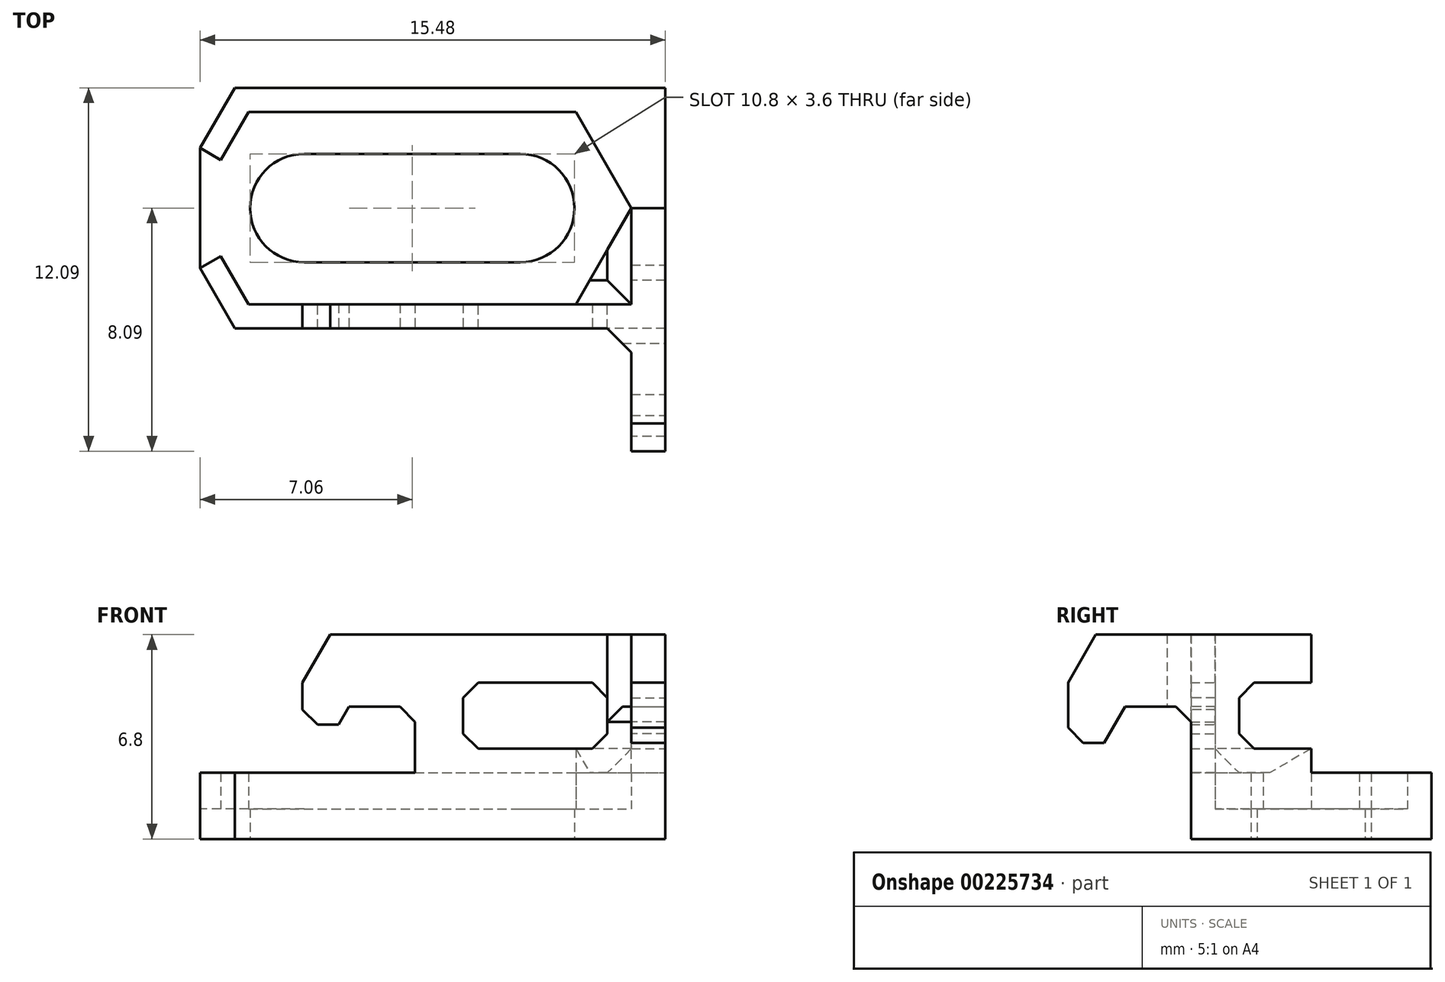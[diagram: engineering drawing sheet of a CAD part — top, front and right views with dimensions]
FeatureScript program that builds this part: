
annotation { "Feature Type Name" : "Feature", "Feature Type Description" : "" }
export const myFeature = defineFeature(function(context is Context, id is Id, definition is map)
    precondition{}
    {
        {
            var Q0;
            Q0=qCreatedBy(makeId("Top.planeOp"),FACE);
            var sketch = newSketch(context, id + "F0", { "sketchPlane" : qUnion([Q0])});
            skCircle(sketch, "E0.cCircle", {"center": v(0, 0) * mm, "radius": 4 * mm, "construction": true});
            skLineSegment(sketch, "E0.0", {"start": v(-2.3, 4) * mm, "end": v(4.82, 4) * mm});
            skLineSegment(sketch, "E0.1", {"start": v(2.3, 4) * mm, "end": v(4.62, 0) * mm, "construction": true});
            skLineSegment(sketch, "E0.2", {"start": v(4.62, 0) * mm, "end": v(2.3, -4) * mm, "construction": true});
            skLineSegment(sketch, "E0.3", {"start": v(4.82, -4) * mm, "end": v(-2.3, -4) * mm});
            skLineSegment(sketch, "E0.4", {"start": v(-2.3, -4) * mm, "end": v(-4.62, 0) * mm, "construction": true});
            skLineSegment(sketch, "E0.5", {"start": v(-4.62, 0) * mm, "end": v(-2.3, 4) * mm, "construction": true});
            skPoint(sketch, "E0.0.midPoint", {"position": v(0, 4) * mm});
            skCircle(sketch, "E1.cCircle", {"center": v(-7.2, 0) * mm, "radius": 4 * mm, "construction": true});
            skLineSegment(sketch, "E1.0", {"start": v(-9.5, 4) * mm, "end": v(-4.9, 4) * mm});
            skLineSegment(sketch, "E1.1", {"start": v(-4.9, 4) * mm, "end": v(-2.58, 0) * mm, "construction": true});
            skLineSegment(sketch, "E1.2", {"start": v(-2.58, 0) * mm, "end": v(-4.9, -4) * mm, "construction": true});
            skLineSegment(sketch, "E1.3", {"start": v(-4.9, -4) * mm, "end": v(-9.5, -4) * mm});
            skLineSegment(sketch, "E1.4", {"start": v(-9.5, -4) * mm, "end": v(-10.66, -2) * mm});
            skLineSegment(sketch, "E1.5", {"start": v(-10.66, 2) * mm, "end": v(-9.5, 4) * mm});
            skPoint(sketch, "E1.0.midPoint", {"position": v(-7.2, 4) * mm});
            skLineSegment(sketch, "E2", {"start": v(-4.9, 4) * mm, "end": v(-2.3, 4) * mm});
            skLineSegment(sketch, "E3", {"start": v(-4.9, -4) * mm, "end": v(-2.3, -4) * mm});
            skLineSegment(sketch, "E4", {"start": v(4.82, 4) * mm, "end": v(4.82, -4) * mm});
            skArc(sketch, "E5", {"start": v(-7.2, 1.8) * mm, "mid": v(-9, 0) * mm, "end": v(-7.2, -1.8) * mm});
            skArc(sketch, "E6", {"start": v(0, -1.8) * mm, "mid": v(1.8, 0) * mm, "end": v(0, 1.8) * mm});
            skLineSegment(sketch, "E7", {"start": v(-10.66, 2) * mm, "end": v(-10.66, -2) * mm});
            skPoint(sketch, "E8.orphan", {"position": v(-11.82, 0) * mm});
            skLineSegment(sketch, "E9", {"start": v(-7.2, 1.8) * mm, "end": v(0, 1.8) * mm});
            skPoint(sketch, "E9.endSnap0", {"position": v(-3.74, 2) * mm});
            skLineSegment(sketch, "E10", {"start": v(-7.2, -1.8) * mm, "end": v(0, -1.8) * mm});
            skSolve(sketch);
        }
        {
            var Q0;
            Q0=qSketchRegion(id+"F0",true);
            extrude(context, id + "F1", {"entities" : qUnion([Q0]), "depth" : 1 * mm});
        }
        {
            var Q0;
            Q0=qCreatedBy(makeId("Top.planeOp"),FACE);
            var sketch = newSketch(context, id + "F2", { "sketchPlane" : qUnion([Q0])});
            skCircle(sketch, "E11.cCircle", {"center": v(-7.2, 0) * mm, "radius": 3.2 * mm, "construction": true});
            skLineSegment(sketch, "E11.0", {"start": v(-9.05, 3.2) * mm, "end": v(-5.35, 3.2) * mm});
            skLineSegment(sketch, "E11.1", {"start": v(-5.35, 3.2) * mm, "end": v(-3.5, 0) * mm, "construction": true});
            skLineSegment(sketch, "E11.2", {"start": v(-3.5, 0) * mm, "end": v(-5.35, -3.2) * mm, "construction": true});
            skLineSegment(sketch, "E11.3", {"start": v(-5.35, -3.2) * mm, "end": v(-9.05, -3.2) * mm});
            skLineSegment(sketch, "E11.4", {"start": v(-9.05, -3.2) * mm, "end": v(-9.97, -1.6) * mm});
            skLineSegment(sketch, "E11.5", {"start": v(-9.97, 1.6) * mm, "end": v(-9.05, 3.2) * mm});
            skPoint(sketch, "E11.0.midPoint", {"position": v(-7.2, 3.2) * mm});
            skCircle(sketch, "E12.cCircle", {"center": v(0, 0) * mm, "radius": 3.2 * mm, "construction": true});
            skLineSegment(sketch, "E12.0", {"start": v(-1.85, 3.2) * mm, "end": v(1.85, 3.2) * mm});
            skLineSegment(sketch, "E12.1", {"start": v(1.85, 3.2) * mm, "end": v(3.7, 0) * mm});
            skLineSegment(sketch, "E12.2", {"start": v(3.7, 0) * mm, "end": v(1.85, -3.2) * mm});
            skLineSegment(sketch, "E12.3", {"start": v(1.85, -3.2) * mm, "end": v(-1.85, -3.2) * mm});
            skLineSegment(sketch, "E12.4", {"start": v(-1.85, -3.2) * mm, "end": v(-3.7, 0) * mm, "construction": true});
            skLineSegment(sketch, "E12.5", {"start": v(-3.7, 0) * mm, "end": v(-1.85, 3.2) * mm, "construction": true});
            skPoint(sketch, "E12.0.midPoint", {"position": v(0, 3.2) * mm});
            skLineSegment(sketch, "E13.0", {"start": v(-9.5, 4) * mm, "end": v(4.82, 4) * mm});
            skLineSegment(sketch, "E13.1", {"start": v(4.82, 4) * mm, "end": v(4.82, -4) * mm});
            skLineSegment(sketch, "E13.2", {"start": v(4.82, -4) * mm, "end": v(-9.5, -4) * mm});
            skLineSegment(sketch, "E13.3", {"start": v(-9.5, -4) * mm, "end": v(-10.66, -2) * mm});
            skLineSegment(sketch, "E13.4", {"start": v(-10.66, 2) * mm, "end": v(-9.5, 4) * mm});
            skLineSegment(sketch, "E14", {"start": v(-10.66, 2) * mm, "end": v(-9.97, 1.6) * mm});
            skLineSegment(sketch, "E15", {"start": v(-10.66, -2) * mm, "end": v(-9.97, -1.6) * mm});
            skPoint(sketch, "E16.orphan", {"position": v(-10.9, 0) * mm});
            skLineSegment(sketch, "E17", {"start": v(-5.35, 3.2) * mm, "end": v(-1.85, 3.2) * mm});
            skLineSegment(sketch, "E18", {"start": v(-5.35, -3.2) * mm, "end": v(-1.85, -3.2) * mm});
            skSolve(sketch);
        }
        {
            var Q0;
            Q0=qSketchRegion(id+"F2",true);
            var Q1;
            Q1=qConstructionFilter(qBodyType(qCreatedBy(id+"F2",EDGE),BodyType.WIRE),ConstructionObject.NO);
            extrude(context, id + "F3", {"entities" : qUnion([Q0]), "operationType" : NewBodyOperationType.ADD, "surfaceEntities" : qUnion([Q1]), "depth" : 2.2 * mm});
        }
        {
            var Q0;
            Q0=makeQuery(id+"F3.boolean.opBoolean","MERGE",FACE,{"derivedFrom":[makeQuery(id+"F1.opExtrude","SWEPT_FACE",FACE,{"disambiguationData":[OSD([sQuery(id+"F0.wireOp",EDGE,"E4")])]}),makeQuery(id+"F3.opExtrude","SWEPT_FACE",FACE,{"disambiguationData":[OSD([sQuery(id+"F2.wireOp",EDGE,"E13.1")])]})]});
            var sketch = newSketch(context, id + "F4", { "sketchPlane" : qUnion([Q0])});
            skLineSegment(sketch, "E19.bottom", {"start": v(-2.4, 5.2) * mm, "end": v(0, 5.2) * mm});
            skLineSegment(sketch, "E19.top", {"start": v(-2.4, 3) * mm, "end": v(0, 3) * mm});
            skLineSegment(sketch, "E19.left", {"start": v(-2.4, 5.2) * mm, "end": v(-2.4, 3) * mm});
            skLineSegment(sketch, "E20", {"start": v(0, 6.8) * mm, "end": v(0, 5.2) * mm});
            skLineSegment(sketch, "E21", {"start": v(-8.1, 6.8) * mm, "end": v(0, 6.8) * mm});
            skLineSegment(sketch, "E22", {"start": v(-8.1, 6.8) * mm, "end": v(-8.1, 3.2) * mm});
            skLineSegment(sketch, "E23", {"start": v(-6.9, 3.2) * mm, "end": v(-8.1, 3.2) * mm});
            skLineSegment(sketch, "E24", {"start": v(-6.9, 3.2) * mm, "end": v(-6.2, 4.4) * mm});
            skLineSegment(sketch, "E25", {"start": v(-6.2, 4.4) * mm, "end": v(-4, 4.4) * mm});
            skLineSegment(sketch, "E26", {"start": v(-4, 4.4) * mm, "end": v(-4, 2.2) * mm});
            skPoint(sketch, "E27.orphan", {"position": v(0, 3) * mm});
            skLineSegment(sketch, "E28.trimOffspring", {"start": v(0, 3) * mm, "end": v(0, 0) * mm});
            skLineSegment(sketch, "E29.0", {"start": v(-4, 2.2) * mm, "end": v(-4, 0) * mm});
            skLineSegment(sketch, "E30.0", {"start": v(0, 0) * mm, "end": v(-4, 0) * mm});
            skPoint(sketch, "E31.orphan", {"position": v(4, 0) * mm});
            skSolve(sketch);
        }
        {
            var Q0;
            Q0=qSketchRegion(id+"F4",true);
            var Q1;
            Q1=makeQuery(id+"F3.opExtrude","CAP_VERTEX",VERTEX,{"disambiguationData":[OSD([sQuery(id+"F2.wireOp",EDGE,"E12.1"),sQuery(id+"F2.wireOp",EDGE,"E12.2")])],"isStart":false});
            extrude(context, id + "F5", {"entities" : qUnion([Q0]), "operationType" : NewBodyOperationType.ADD, "endBound" : BoundingType.UP_TO_VERTEX, "oppositeDirection" : true, "endBoundEntityVertex" : qUnion([Q1]), "depth" : 25 * mm});
        }
        {
            var Q0;
            Q0=makeQuery(id+"F5.boolean.opBoolean","MERGE",FACE,{"derivedFrom":[makeQuery(id+"F3.boolean.opBoolean","MERGE",FACE,{"derivedFrom":[makeQuery(id+"F1.opExtrude","SWEPT_FACE",FACE,{"disambiguationData":[OSD([sQuery(id+"F0.wireOp",EDGE,"E0.3"),sQuery(id+"F0.wireOp",EDGE,"E1.3"),sQuery(id+"F0.wireOp",EDGE,"E3")])]}),makeQuery(id+"F3.opExtrude","SWEPT_FACE",FACE,{"disambiguationData":[OSD([sQuery(id+"F2.wireOp",EDGE,"E13.2")])]})]}),makeQuery(id+"F5.opExtrude","SWEPT_FACE",FACE,{"disambiguationData":[OSD([sQuery(id+"F4.wireOp",EDGE,"E26"),sQuery(id+"F4.wireOp",EDGE,"E29.0")])]})]});
            var sketch = newSketch(context, id + "F6", { "sketchPlane" : qUnion([Q0])});
            skLineSegment(sketch, "E32.bottom", {"start": v(-1.9, 5.2) * mm, "end": v(0.5, 5.2) * mm});
            skLineSegment(sketch, "E32.top", {"start": v(-1.9, 3) * mm, "end": v(0.5, 3) * mm});
            skLineSegment(sketch, "E32.left", {"start": v(-1.9, 5.2) * mm, "end": v(-1.9, 3) * mm});
            skLineSegment(sketch, "E33", {"start": v(0.5, 6.8) * mm, "end": v(0.5, 5.2) * mm, "construction": true});
            skLineSegment(sketch, "E34", {"start": v(-7.25, 6.8) * mm, "end": v(3.7, 6.8) * mm});
            skLineSegment(sketch, "E35", {"start": v(-7.25, 6.8) * mm, "end": v(-7.25, 3.8) * mm});
            skLineSegment(sketch, "E36", {"start": v(-6.05, 3.8) * mm, "end": v(-7.25, 3.8) * mm});
            skLineSegment(sketch, "E37", {"start": v(-6.05, 3.8) * mm, "end": v(-5.7, 4.4) * mm});
            skLineSegment(sketch, "E38", {"start": v(-5.7, 4.4) * mm, "end": v(-3.5, 4.4) * mm});
            skLineSegment(sketch, "E39", {"start": v(-3.5, 4.4) * mm, "end": v(-3.5, 0) * mm});
            skPoint(sketch, "E40.orphan", {"position": v(0.5, 3) * mm});
            skLineSegment(sketch, "E41.trimOffspring", {"start": v(0.5, 3) * mm, "end": v(0.5, 0) * mm, "construction": true});
            skLineSegment(sketch, "E42.0", {"start": v(3.7, 0) * mm, "end": v(-3.5, 0) * mm});
            skLineSegment(sketch, "E43", {"start": v(0.5, 5.2) * mm, "end": v(2.9, 5.2) * mm});
            skLineSegment(sketch, "E44", {"start": v(2.9, 5.2) * mm, "end": v(2.9, 3) * mm});
            skLineSegment(sketch, "E45", {"start": v(2.9, 3) * mm, "end": v(0.5, 3) * mm});
            skLineSegment(sketch, "E46.0", {"start": v(3.7, 0) * mm, "end": v(3.7, 6.8) * mm});
            skPoint(sketch, "E47.orphan", {"position": v(3.7, 5.2) * mm});
            skSolve(sketch);
        }
        {
            var Q0;
            Q0=qSketchRegion(id+"F6",true);
            extrude(context, id + "F7", {"entities" : qUnion([Q0]), "operationType" : NewBodyOperationType.ADD, "oppositeDirection" : true, "depth" : 0.8 * mm});
        }
        {
            var Q0;
            Q0=makeQuery(id+"F5.boolean.opBoolean","INTERSECT",EDGE,{"derivedFrom":[makeQuery(id+"F3.opExtrude","CAP_FACE",FACE,{"disambiguationData":[OSD([sQuery(id+"F2.wireOp",EDGE,"E11.0"),sQuery(id+"F2.wireOp",EDGE,"E11.3"),sQuery(id+"F2.wireOp",EDGE,"E11.4"),sQuery(id+"F2.wireOp",EDGE,"E11.5"),sQuery(id+"F2.wireOp",EDGE,"E12.0"),sQuery(id+"F2.wireOp",EDGE,"E12.1"),sQuery(id+"F2.wireOp",EDGE,"E12.2"),sQuery(id+"F2.wireOp",EDGE,"E12.3"),sQuery(id+"F2.wireOp",EDGE,"E13.0"),sQuery(id+"F2.wireOp",EDGE,"E13.1"),sQuery(id+"F2.wireOp",EDGE,"E13.2"),sQuery(id+"F2.wireOp",EDGE,"E13.3"),sQuery(id+"F2.wireOp",EDGE,"E13.4"),sQuery(id+"F2.wireOp",EDGE,"E14"),sQuery(id+"F2.wireOp",EDGE,"E15"),sQuery(id+"F2.wireOp",EDGE,"E17"),sQuery(id+"F2.wireOp",EDGE,"E18")])],"isStart":false}),makeQuery(id+"F5.opExtrude","CAP_FACE",FACE,{"disambiguationData":[OSD([sQuery(id+"F4.wireOp",EDGE,"E19.bottom"),sQuery(id+"F4.wireOp",EDGE,"E19.top"),sQuery(id+"F4.wireOp",EDGE,"E19.left"),sQuery(id+"F4.wireOp",EDGE,"E20"),sQuery(id+"F4.wireOp",EDGE,"E21"),sQuery(id+"F4.wireOp",EDGE,"E22"),sQuery(id+"F4.wireOp",EDGE,"E23"),sQuery(id+"F4.wireOp",EDGE,"E24"),sQuery(id+"F4.wireOp",EDGE,"E25"),sQuery(id+"F4.wireOp",EDGE,"E26"),sQuery(id+"F4.wireOp",EDGE,"E28.trimOffspring"),sQuery(id+"F4.wireOp",EDGE,"E29.0"),sQuery(id+"F4.wireOp",EDGE,"E30.0")])],"isStart":false})]});
            var Q1;
            {var subQ0=sQuery(id+"F4.wireOp",EDGE,"E30.0");var subQ1=sQuery(id+"F4.wireOp",EDGE,"E29.0");var subQ2=sQuery(id+"F4.wireOp",EDGE,"E28.trimOffspring");var subQ3=sQuery(id+"F4.wireOp",EDGE,"E26");var subQ4=sQuery(id+"F4.wireOp",EDGE,"E25");var subQ5=sQuery(id+"F4.wireOp",EDGE,"E24");var subQ6=sQuery(id+"F4.wireOp",EDGE,"E23");var subQ7=sQuery(id+"F4.wireOp",EDGE,"E22");var subQ8=sQuery(id+"F4.wireOp",EDGE,"E21");var subQ9=sQuery(id+"F4.wireOp",EDGE,"E20");var subQ10=sQuery(id+"F4.wireOp",EDGE,"E19.left");var subQ11=sQuery(id+"F4.wireOp",EDGE,"E19.top");var subQ12=sQuery(id+"F4.wireOp",EDGE,"E19.bottom");var subQ13=sQuery(id+"F2.wireOp",EDGE,"E13.1");var subQ14=sQuery(id+"F2.wireOp",EDGE,"E13.0");var subQ15=sQuery(id+"F2.wireOp",EDGE,"E12.2");var subQ16=sQuery(id+"F2.wireOp",EDGE,"E12.1");var subQ17=sQuery(id+"F2.wireOp",EDGE,"E17");var subQ18=sQuery(id+"F2.wireOp",EDGE,"E12.0");var subQ19=sQuery(id+"F2.wireOp",EDGE,"E11.0");var subQ20=sQuery(id+"F2.wireOp",EDGE,"E14");var subQ21=sQuery(id+"F2.wireOp",EDGE,"E13.4");var subQ22=sQuery(id+"F2.wireOp",EDGE,"E11.5");var subQ23=makeQuery(id+"F3.opExtrude","CAP_FACE",FACE,{"disambiguationData":[OSD([subQ19,sQuery(id+"F2.wireOp",EDGE,"E11.3"),sQuery(id+"F2.wireOp",EDGE,"E11.4"),subQ22,subQ18,subQ16,subQ15,sQuery(id+"F2.wireOp",EDGE,"E12.3"),subQ14,subQ13,sQuery(id+"F2.wireOp",EDGE,"E13.2"),sQuery(id+"F2.wireOp",EDGE,"E13.3"),subQ21,subQ20,sQuery(id+"F2.wireOp",EDGE,"E15"),subQ17,sQuery(id+"F2.wireOp",EDGE,"E18")])],"isStart":false});Q1=makeQuery(id+"F8ARvuKSKwCrkYK_1.1.F5.boolean.opBoolean","INTERSECT",EDGE,{"derivedFrom":[makeQuery(id+"F5.boolean.opBoolean","SPLIT",FACE,{"disambiguationData":[TD([makeQuery(id+"F1.opExtrude","SWEPT_FACE",FACE,{"disambiguationData":[OSD([sQuery(id+"F0.wireOp",EDGE,"E1.5")])]})])],"derivedFrom":subQ23}),makeQuery(id+"F8ARvuKSKwCrkYK_1.1.F5.opExtrude","CAP_FACE",FACE,{"disambiguationData":[OSD([subQ12,subQ11,subQ10,subQ9,subQ8,subQ7,subQ6,subQ5,subQ4,subQ3,subQ2,subQ1,subQ0])],"isStart":false})]});}
            var Q2;
            {var subQ0=sQuery(id+"F2.wireOp",EDGE,"E13.3");var subQ2=sQuery(id+"F2.wireOp",EDGE,"E13.2");var subQ5=sQuery(id+"F2.wireOp",EDGE,"E12.2");var subQ6=sQuery(id+"F2.wireOp",EDGE,"E12.1");var subQ7=sQuery(id+"F2.wireOp",EDGE,"E11.4");var subQ8=sQuery(id+"F2.wireOp",EDGE,"E18");var subQ9=sQuery(id+"F2.wireOp",EDGE,"E15");var subQ10=sQuery(id+"F2.wireOp",EDGE,"E12.3");var subQ11=sQuery(id+"F2.wireOp",EDGE,"E11.3");var subQ12=makeQuery(id+"F3.opExtrude","CAP_FACE",FACE,{"disambiguationData":[OSD([sQuery(id+"F2.wireOp",EDGE,"E11.0"),subQ11,subQ7,sQuery(id+"F2.wireOp",EDGE,"E11.5"),sQuery(id+"F2.wireOp",EDGE,"E12.0"),subQ6,subQ5,subQ10,sQuery(id+"F2.wireOp",EDGE,"E13.0"),sQuery(id+"F2.wireOp",EDGE,"E13.1"),subQ2,subQ0,sQuery(id+"F2.wireOp",EDGE,"E13.4"),sQuery(id+"F2.wireOp",EDGE,"E14"),subQ9,sQuery(id+"F2.wireOp",EDGE,"E17"),subQ8])],"isStart":false});Q2=makeQuery(id+"F7.boolean.opBoolean","INTERSECT",EDGE,{"derivedFrom":[makeQuery(id+"F5.boolean.opBoolean","SPLIT",FACE,{"disambiguationData":[TD([makeQuery(id+"F1.opExtrude","SWEPT_FACE",FACE,{"disambiguationData":[OSD([sQuery(id+"F0.wireOp",EDGE,"E1.4")])]})])],"derivedFrom":subQ12}),makeQuery(id+"F7.opExtrude","CAP_FACE",FACE,{"disambiguationData":[OSD([sQuery(id+"F6.wireOp",EDGE,"E32.bottom"),sQuery(id+"F6.wireOp",EDGE,"E32.top"),sQuery(id+"F6.wireOp",EDGE,"E32.left"),sQuery(id+"F6.wireOp",EDGE,"E34"),sQuery(id+"F6.wireOp",EDGE,"E35"),sQuery(id+"F6.wireOp",EDGE,"E36"),sQuery(id+"F6.wireOp",EDGE,"E37"),sQuery(id+"F6.wireOp",EDGE,"E38"),sQuery(id+"F6.wireOp",EDGE,"E39"),sQuery(id+"F6.wireOp",EDGE,"E42.0"),sQuery(id+"F6.wireOp",EDGE,"E43"),sQuery(id+"F6.wireOp",EDGE,"E44"),sQuery(id+"F6.wireOp",EDGE,"E45"),sQuery(id+"F6.wireOp",EDGE,"E46.0")])],"isStart":false})]});}
            var Q3;
            Q3=makeQuery(id+"F7.opExtrude","CAP_EDGE",EDGE,{"disambiguationData":[OSD([sQuery(id+"F6.wireOp",EDGE,"E46.0")])],"isStart":false});
            var Q4;
            Q4=makeQuery(id+"F7.opExtrude","CAP_EDGE",EDGE,{"disambiguationData":[OSD([sQuery(id+"F6.wireOp",EDGE,"E46.0")])],"isStart":true});
            chamfer(context, id + "F8", {"entities" : qUnion([Q0, Q1, Q2, Q3, Q4]), "width" : 0.8 * mm, "tangentPropagation" : true});
        }
        {
            var Q0;
            Q0=makeQuery(id+"F5.opExtrude","SWEPT_EDGE",EDGE,{"disambiguationData":[OSD([sQuery(id+"F4.wireOp",EDGE,"E21"),sQuery(id+"F4.wireOp",EDGE,"E22")])]});
            var Q1;
            Q1=makeQuery(id+"F8ARvuKSKwCrkYK_1.1.F5.opExtrude","SWEPT_EDGE",EDGE,{"disambiguationData":[OSD([sQuery(id+"F4.wireOp",EDGE,"E21"),sQuery(id+"F4.wireOp",EDGE,"E22")])]});
            var Q2;
            Q2=makeQuery(id+"F7.opExtrude","SWEPT_EDGE",EDGE,{"disambiguationData":[OSD([sQuery(id+"F6.wireOp",EDGE,"E34"),sQuery(id+"F6.wireOp",EDGE,"E35")])]});
            chamfer(context, id + "F9", {"entities" : qUnion([Q0, Q1, Q2]), "chamferType" : ChamferType.OFFSET_ANGLE, "width" : 1.6 * mm, "oppositeDirection" : true, "angle" : 30 * degree, "tangentPropagation" : true});
        }
        {
            var Q0;
            Q0=makeQuery(id+"F5.opExtrude","SWEPT_EDGE",EDGE,{"disambiguationData":[OSD([sQuery(id+"F4.wireOp",EDGE,"E22"),sQuery(id+"F4.wireOp",EDGE,"E23")])]});
            var Q1;
            Q1=makeQuery(id+"F8ARvuKSKwCrkYK_1.1.F5.opExtrude","SWEPT_EDGE",EDGE,{"disambiguationData":[OSD([sQuery(id+"F4.wireOp",EDGE,"E22"),sQuery(id+"F4.wireOp",EDGE,"E23")])]});
            var Q2;
            Q2=makeQuery(id+"F5.opExtrude","SWEPT_EDGE",EDGE,{"disambiguationData":[OSD([sQuery(id+"F4.wireOp",EDGE,"E25"),sQuery(id+"F4.wireOp",EDGE,"E26")])]});
            var Q3;
            Q3=makeQuery(id+"F8ARvuKSKwCrkYK_1.1.F5.opExtrude","SWEPT_EDGE",EDGE,{"disambiguationData":[OSD([sQuery(id+"F4.wireOp",EDGE,"E25"),sQuery(id+"F4.wireOp",EDGE,"E26")])]});
            var Q4;
            Q4=makeQuery(id+"F5.opExtrude","SWEPT_EDGE",EDGE,{"disambiguationData":[OSD([sQuery(id+"F4.wireOp",EDGE,"E19.bottom"),sQuery(id+"F4.wireOp",EDGE,"E19.left")])]});
            var Q5;
            Q5=makeQuery(id+"F5.opExtrude","SWEPT_EDGE",EDGE,{"disambiguationData":[OSD([sQuery(id+"F4.wireOp",EDGE,"E19.top"),sQuery(id+"F4.wireOp",EDGE,"E19.left")])]});
            var Q6;
            Q6=makeQuery(id+"F8ARvuKSKwCrkYK_1.1.F5.opExtrude","SWEPT_EDGE",EDGE,{"disambiguationData":[OSD([sQuery(id+"F4.wireOp",EDGE,"E19.bottom"),sQuery(id+"F4.wireOp",EDGE,"E19.left")])]});
            var Q7;
            Q7=makeQuery(id+"F8ARvuKSKwCrkYK_1.1.F5.opExtrude","SWEPT_EDGE",EDGE,{"disambiguationData":[OSD([sQuery(id+"F4.wireOp",EDGE,"E19.top"),sQuery(id+"F4.wireOp",EDGE,"E19.left")])]});
            var Q8;
            Q8=makeQuery(id+"F7.opExtrude","SWEPT_EDGE",EDGE,{"disambiguationData":[OSD([sQuery(id+"F6.wireOp",EDGE,"E43"),sQuery(id+"F6.wireOp",EDGE,"E44")])]});
            var Q9;
            Q9=makeQuery(id+"F7.opExtrude","SWEPT_EDGE",EDGE,{"disambiguationData":[OSD([sQuery(id+"F6.wireOp",EDGE,"E32.bottom"),sQuery(id+"F6.wireOp",EDGE,"E32.left")])]});
            var Q10;
            Q10=makeQuery(id+"F7.opExtrude","SWEPT_EDGE",EDGE,{"disambiguationData":[OSD([sQuery(id+"F6.wireOp",EDGE,"E32.top"),sQuery(id+"F6.wireOp",EDGE,"E32.left")])]});
            var Q11;
            Q11=makeQuery(id+"F7.opExtrude","SWEPT_EDGE",EDGE,{"disambiguationData":[OSD([sQuery(id+"F6.wireOp",EDGE,"E44"),sQuery(id+"F6.wireOp",EDGE,"E45")])]});
            var Q12;
            Q12=makeQuery(id+"F7.opExtrude","SWEPT_EDGE",EDGE,{"disambiguationData":[OSD([sQuery(id+"F6.wireOp",EDGE,"E35"),sQuery(id+"F6.wireOp",EDGE,"E36")])]});
            var Q13;
            Q13=makeQuery(id+"F7.opExtrude","SWEPT_EDGE",EDGE,{"disambiguationData":[OSD([sQuery(id+"F6.wireOp",EDGE,"E38"),sQuery(id+"F6.wireOp",EDGE,"E39")])]});
            chamfer(context, id + "F10", {"entities" : qUnion([Q0, Q1, Q2, Q3, Q4, Q5, Q6, Q7, Q8, Q9, Q10, Q11, Q12, Q13]), "width" : 0.5 * mm, "tangentPropagation" : true});
        }
    });
